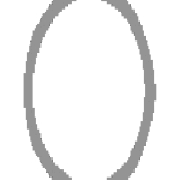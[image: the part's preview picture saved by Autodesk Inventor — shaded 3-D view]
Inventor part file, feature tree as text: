
AUTODESK INVENTOR PART (.ipt)
format: ipt  version: 2021 (Build 250183000, 183)  size: 109,568 bytes
history: native  units: in
note: dims shown in document units (in); Inventor stores cm internally (conversion verified against a paired STEP export)
features: other x4, sketch x3, plane x1
ambient origin geometry x8: Origin, YZ Plane, XZ Plane, XY Plane, X Axis, Y Axis, Z Axis, Center Point
bodies: Solid1 (feature_tree), Body (feature_tree)
feature tree (8):
  other  "Driven Length"
  other  "Frame Generator"
  other  "Start Plane"
  other  "End Plane"
  sketch  "Sketch"  dims[d2=13.2634in d4=-0.0in d5=13.2634in d6=0.12in d7=0.0in d8=90.0deg d9=13.2634in]
  sketch  "Sketch2"  dims[d0=1.0in]
  plane  "Work Plane3"
  sketch  "Sketch3"  dims[d1=0.065in]
